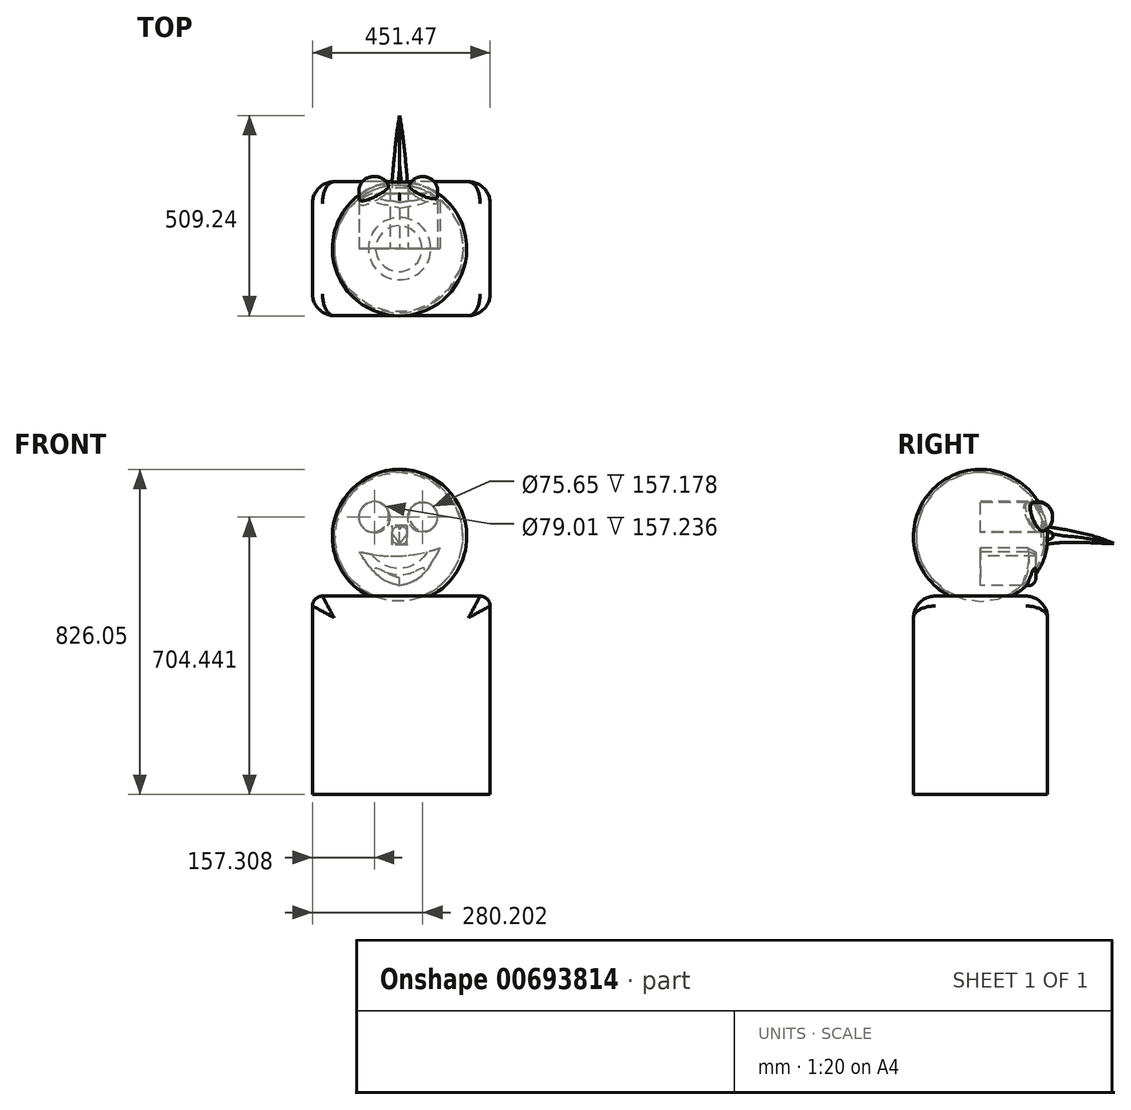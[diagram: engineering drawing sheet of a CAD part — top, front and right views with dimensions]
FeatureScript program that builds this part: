
annotation { "Feature Type Name" : "Feature", "Feature Type Description" : "" }
export const myFeature = defineFeature(function(context is Context, id is Id, definition is map)
    precondition{}
    {
        {
            var Q0;
            Q0=qCreatedBy(makeId("Front.planeOp"),FACE);
            var sketch = newSketch(context, id + "F0", { "sketchPlane" : qUnion([Q0])});
            skCircle(sketch, "E0", {"center": v(0, 0) * mm, "radius": 170.72 * mm});
            skLineSegment(sketch, "E1", {"start": v(-245.6, 0) * mm, "end": v(227.44, 0) * mm, "construction": true});
            skSolve(sketch);
        }
        {
            var Q0;
            Q0=makeQuery(id+"F0.imprint","IMPRINT",FACE,{"disambiguationData":[TD([[makeQuery(id+"F0.imprint","IMPRINT",EDGE,{"derivedFrom":sQuery(id+"F0.wireOp",EDGE,"E0")}),1.0]])]});
            var sketch = newSketch(context, id + "F1", { "sketchPlane" : qUnion([Q0])});
            skLineSegment(sketch, "E2", {"start": v(-217.62, 0) * mm, "end": v(207.45, 0) * mm});
            skSolve(sketch);
        }
        {
            var Q0;
            {var subQ0=sQuery(id+"F1.wireOp",EDGE,"E2");var subQ1=makeQuery(id+"F0.imprint","IMPRINT",EDGE,{"derivedFrom":sQuery(id+"F0.wireOp",EDGE,"E0")});var subQ2=makeQuery(id+"F1.imprint","INTERSECT",VERTEX,{"disambiguationData":[OD(0.0)],"derivedFrom":[subQ1,subQ0]});Q0=makeQuery(id+"F1.imprint","IMPRINT",FACE,{"disambiguationData":[TD([[makeQuery(id+"F1.imprint","IMPRINT",EDGE,{"disambiguationData":[TD([[subQ2,-1.0]])],"derivedFrom":subQ0}),1.0]])]});}
            var Q1;
            Q1=sQuery(id+"F1.wireOp",EDGE,"E2");
            revolve(context, id + "F2", {"entities" : qUnion([Q0]), "axis" : qUnion([Q1]), "revolveType" : RevolveType.FULL});
        }
        {
            var Q0;
            Q0=qCreatedBy(makeId("Front.planeOp"),FACE);
            var sketch = newSketch(context, id + "F3", { "sketchPlane" : qUnion([Q0])});
            skLineSegment(sketch, "E3", {"start": v(-244.63, 0) * mm, "end": v(212.5, 0) * mm, "construction": true});
            skLineSegment(sketch, "E4", {"start": v(-187.37, 0) * mm, "end": v(187.83, 0) * mm});
            skArc(sketch, "E5", {"start": v(161.76, 0) * mm, "mid": v(-1.63, 162.2) * mm, "end": v(-165.03, 0) * mm});
            skSolve(sketch);
        }
        {
            var Q0;
            Q0=qSketchRegion(id+"F3",true);
            var Q1;
            Q1=sQuery(id+"F3.wireOp",EDGE,"E4");
            revolve(context, id + "F4", {"operationType" : NewBodyOperationType.REMOVE, "entities" : qUnion([Q0]), "axis" : qUnion([Q1]), "revolveType" : RevolveType.FULL, "oppositeDirection" : true});
        }
        {
            var Q0;
            Q0=qCreatedBy(makeId("Right.planeOp"),FACE);
            var sketch = newSketch(context, id + "F5", { "sketchPlane" : qUnion([Q0])});
            skFitSpline(sketch, "E6", {"points": [v(153.24, 27.46) * mm, v(297.74, 0) * mm, v(380.54, -28.78) * mm], "startDerivative": vector(274.67, -43.75) * mm, "endDerivative": vector(175.67, -69.85) * mm});
            skFitSpline(sketch, "E7", {"points": [v(380.54, -28.78) * mm, v(227.45, -14.72) * mm, v(153.24, -21.75) * mm], "startDerivative": vector(-282.95, 35.93) * mm, "endDerivative": vector(-164.57, -25.53) * mm});
            skLineSegment(sketch, "E8", {"start": v(153.24, 27.46) * mm, "end": v(153.24, -21.75) * mm});
            skSolve(sketch);
        }
        {
            var Q0;
            Q0=qSketchRegion(id+"F5",true);
            extrude(context, id + "F6", {"entities" : qUnion([Q0]), "operationType" : NewBodyOperationType.ADD, "endBound" : BoundingType.SYMMETRIC, "depth" : 38.1 * mm, "offsetDistance" : 25.4 * mm});
        }
        {
            var Q0;
            Q0=qCreatedBy(makeId("Top.planeOp"),FACE);
            var sketch = newSketch(context, id + "F7", { "sketchPlane" : qUnion([Q0])});
            skLineSegment(sketch, "E9", {"start": v(-19.02, 171.68) * mm, "end": v(0, 384.82) * mm});
            skLineSegment(sketch, "E10", {"start": v(0, 384.82) * mm, "end": v(20.21, 171.68) * mm});
            skLineSegment(sketch, "E11", {"start": v(20.21, 171.68) * mm, "end": v(46.72, 222.58) * mm});
            skLineSegment(sketch, "E12", {"start": v(46.72, 222.58) * mm, "end": v(30.82, 444.2) * mm});
            skLineSegment(sketch, "E13", {"start": v(30.82, 444.2) * mm, "end": v(-83.7, 375.28) * mm});
            skLineSegment(sketch, "E14", {"start": v(-83.7, 375.28) * mm, "end": v(-19.02, 171.68) * mm});
            skSolve(sketch);
        }
        {
            var Q0;
            Q0=qSketchRegion(id+"F7",true);
            extrude(context, id + "F8", {"entities" : qUnion([Q0]), "operationType" : NewBodyOperationType.REMOVE, "endBound" : BoundingType.SYMMETRIC, "depth" : 548.64 * mm, "offsetDistance" : 25.4 * mm});
        }
        {
            var Q0;
            {var subQ2=sQuery(id+"F5.wireOp",EDGE,"E6");Q0=makeQuery(id+"F8.boolean.opBoolean","INTERSECT",EDGE,{"derivedFrom":[makeQuery(id+"F6.boolean.opBoolean","SPLIT",FACE,{"disambiguationData":[TD([makeQuery(id+"F2.opRevolve","SWEPT_FACE",FACE,{"disambiguationData":[OSD([sQuery(id+"F0.wireOp",EDGE,"E0")])]})])],"derivedFrom":makeQuery(id+"F6.opExtrude","SWEPT_FACE",FACE,{"disambiguationData":[OSD([subQ2])]})}),makeQuery(id+"F8.opExtrude","SWEPT_FACE",FACE,{"disambiguationData":[OSD([sQuery(id+"F7.wireOp",EDGE,"E9")])]})]});}
            var Q1;
            {var subQ2=sQuery(id+"F5.wireOp",EDGE,"E7");Q1=makeQuery(id+"F8.boolean.opBoolean","INTERSECT",EDGE,{"derivedFrom":[makeQuery(id+"F6.boolean.opBoolean","SPLIT",FACE,{"disambiguationData":[TD([makeQuery(id+"F2.opRevolve","SWEPT_FACE",FACE,{"disambiguationData":[OSD([sQuery(id+"F0.wireOp",EDGE,"E0")])]})])],"derivedFrom":makeQuery(id+"F6.opExtrude","SWEPT_FACE",FACE,{"disambiguationData":[OSD([subQ2])]})}),makeQuery(id+"F8.opExtrude","SWEPT_FACE",FACE,{"disambiguationData":[OSD([sQuery(id+"F7.wireOp",EDGE,"E9")])]})]});}
            var Q2;
            {var subQ2=sQuery(id+"F5.wireOp",EDGE,"E6");Q2=makeQuery(id+"F8.boolean.opBoolean","INTERSECT",EDGE,{"derivedFrom":[makeQuery(id+"F6.boolean.opBoolean","SPLIT",FACE,{"disambiguationData":[TD([makeQuery(id+"F2.opRevolve","SWEPT_FACE",FACE,{"disambiguationData":[OSD([sQuery(id+"F0.wireOp",EDGE,"E0")])]})])],"derivedFrom":makeQuery(id+"F6.opExtrude","SWEPT_FACE",FACE,{"disambiguationData":[OSD([subQ2])]})}),makeQuery(id+"F8.opExtrude","SWEPT_FACE",FACE,{"disambiguationData":[OSD([sQuery(id+"F7.wireOp",EDGE,"E10")])]})]});}
            var Q3;
            {var subQ2=sQuery(id+"F5.wireOp",EDGE,"E7");Q3=makeQuery(id+"F8.boolean.opBoolean","INTERSECT",EDGE,{"derivedFrom":[makeQuery(id+"F6.boolean.opBoolean","SPLIT",FACE,{"disambiguationData":[TD([makeQuery(id+"F2.opRevolve","SWEPT_FACE",FACE,{"disambiguationData":[OSD([sQuery(id+"F0.wireOp",EDGE,"E0")])]})])],"derivedFrom":makeQuery(id+"F6.opExtrude","SWEPT_FACE",FACE,{"disambiguationData":[OSD([subQ2])]})}),makeQuery(id+"F8.opExtrude","SWEPT_FACE",FACE,{"disambiguationData":[OSD([sQuery(id+"F7.wireOp",EDGE,"E10")])]})]});}
            fillet(context, id + "F9", {"entities" : qUnion([Q0, Q1, Q2, Q3]), "radius" : 16.32 * mm, "tangentPropagation" : true, "allowEdgeOverflow" : false});
        }
        {
            var Q0;
            Q0=qCreatedBy(makeId("Front.planeOp"),FACE);
            var sketch = newSketch(context, id + "F10", { "sketchPlane" : qUnion([Q0])});
            skCircle(sketch, "E15", {"center": v(58.88, 49.11) * mm, "radius": 37.82 * mm});
            skCircle(sketch, "E16", {"center": v(-64.01, 49.11) * mm, "radius": 39.5 * mm});
            skLineSegment(sketch, "E17", {"start": v(135.7, 49.11) * mm, "end": v(-137.56, 49.11) * mm, "construction": true});
            skSolve(sketch);
        }
        {
            var Q0;
            Q0=qSketchRegion(id+"F10",true);
            extrude(context, id + "F11", {"entities" : qUnion([Q0]), "operationType" : NewBodyOperationType.ADD, "oppositeDirection" : true, "depth" : 182.88 * mm, "offsetDistance" : 25.4 * mm});
        }
        {
            var Q0;
            Q0=makeQuery(id+"F11.opExtrude","CAP_EDGE",EDGE,{"disambiguationData":[OSD([sQuery(id+"F10.wireOp",EDGE,"E15")])],"isStart":false});
            var Q1;
            Q1=makeQuery(id+"F11.opExtrude","CAP_EDGE",EDGE,{"disambiguationData":[OSD([sQuery(id+"F10.wireOp",EDGE,"E16")])],"isStart":false});
            fillet(context, id + "F12", {"entities" : qUnion([Q0, Q1]), "radius" : 36.8 * mm, "tangentPropagation" : true, "allowEdgeOverflow" : false});
        }
        {
            var Q0;
            Q0=qCreatedBy(makeId("Front.planeOp"),FACE);
            var sketch = newSketch(context, id + "F13", { "sketchPlane" : qUnion([Q0])});
            skArc(sketch, "E18", {"start": v(-103.11, -38.87) * mm, "mid": v(0.69, -49.56) * mm, "end": v(103.1, -29.56) * mm});
            skFitSpline(sketch, "E19", {"points": [v(103.1, -29.56) * mm, v(50.5, -104.5) * mm, v(0, -124.99) * mm], "startDerivative": vector(-86.75, -156.97) * mm, "endDerivative": vector(-120.93, -28.36) * mm});
            skFitSpline(sketch, "E20", {"points": [v(0, -124.99) * mm, v(-48.65, -104.5) * mm, v(-103.11, -38.87) * mm], "startDerivative": vector(-113.4, 30.94) * mm, "endDerivative": vector(-93.62, 137.07) * mm});
            skSolve(sketch);
        }
        {
            var Q0;
            Q0=qSketchRegion(id+"F13",true);
            extrude(context, id + "F14", {"entities" : qUnion([Q0]), "operationType" : NewBodyOperationType.ADD, "oppositeDirection" : true, "depth" : 140.46 * mm, "offsetDistance" : 25.4 * mm});
        }
        {
            var Q0;
            Q0=makeQuery(id+"F14.opExtrude","CAP_EDGE",EDGE,{"disambiguationData":[OSD([sQuery(id+"F13.wireOp",EDGE,"E19")])],"isStart":false});
            var Q1;
            Q1=makeQuery(id+"F14.opExtrude","CAP_EDGE",EDGE,{"disambiguationData":[OSD([sQuery(id+"F13.wireOp",EDGE,"E20")])],"isStart":false});
            fillet(context, id + "F15", {"entities" : qUnion([Q0, Q1]), "radius" : 19 * mm, "tangentPropagation" : true, "allowEdgeOverflow" : false});
        }
        {
            var Q0;
            Q0=qCreatedBy(makeId("Front.planeOp"),FACE);
            var sketch = newSketch(context, id + "F16", { "sketchPlane" : qUnion([Q0])});
            skLineSegment(sketch, "E21.bottom", {"start": v(204.75, -151.22) * mm, "end": v(-195.92, -151.22) * mm});
            skLineSegment(sketch, "E21.top", {"start": v(230.15, -655.33) * mm, "end": v(-221.32, -655.33) * mm});
            skLineSegment(sketch, "E21.left", {"start": v(230.15, -176.62) * mm, "end": v(230.15, -655.33) * mm});
            skLineSegment(sketch, "E21.right", {"start": v(-221.32, -176.62) * mm, "end": v(-221.32, -655.33) * mm});
            skPoint(sketch, "E22.visualSharp", {"position": v(230.15, -151.22) * mm});
            skArc(sketch, "E22.filletArc", {"start": v(230.15, -176.62) * mm, "mid": v(222.71, -158.66) * mm, "end": v(204.75, -151.22) * mm});
            skPoint(sketch, "E23.visualSharp", {"position": v(-221.32, -151.22) * mm});
            skArc(sketch, "E23.filletArc", {"start": v(-195.92, -151.22) * mm, "mid": v(-213.88, -158.66) * mm, "end": v(-221.32, -176.62) * mm});
            skSolve(sketch);
        }
        {
            var Q0;
            Q0 = qSketchRegion(id + "F16", true);
            extrude(context, id + "F17", {"entities" : qUnion([Q0]), "operationType" : NewBodyOperationType.ADD, "endBound" : BoundingType.SYMMETRIC, "depth" : 340.36 * mm, "offsetDistance" : 25.4 * mm});
        }
        {
            var Q0;
            Q0=makeQuery(id+"F17.opExtrude","CAP_EDGE",EDGE,{"disambiguationData":[OSD([sQuery(id+"F16.wireOp",EDGE,"E21.bottom")])],"isStart":true});
            var Q1;
            Q1=makeQuery(id+"F17.opExtrude","CAP_EDGE",EDGE,{"disambiguationData":[OSD([sQuery(id+"F16.wireOp",EDGE,"E21.bottom")])],"isStart":false});
            fillet(context, id + "F18", {"entities" : qUnion([Q0, Q1]), "radius" : 55.19 * mm, "tangentPropagation" : true, "allowEdgeOverflow" : false});
        }
    });
